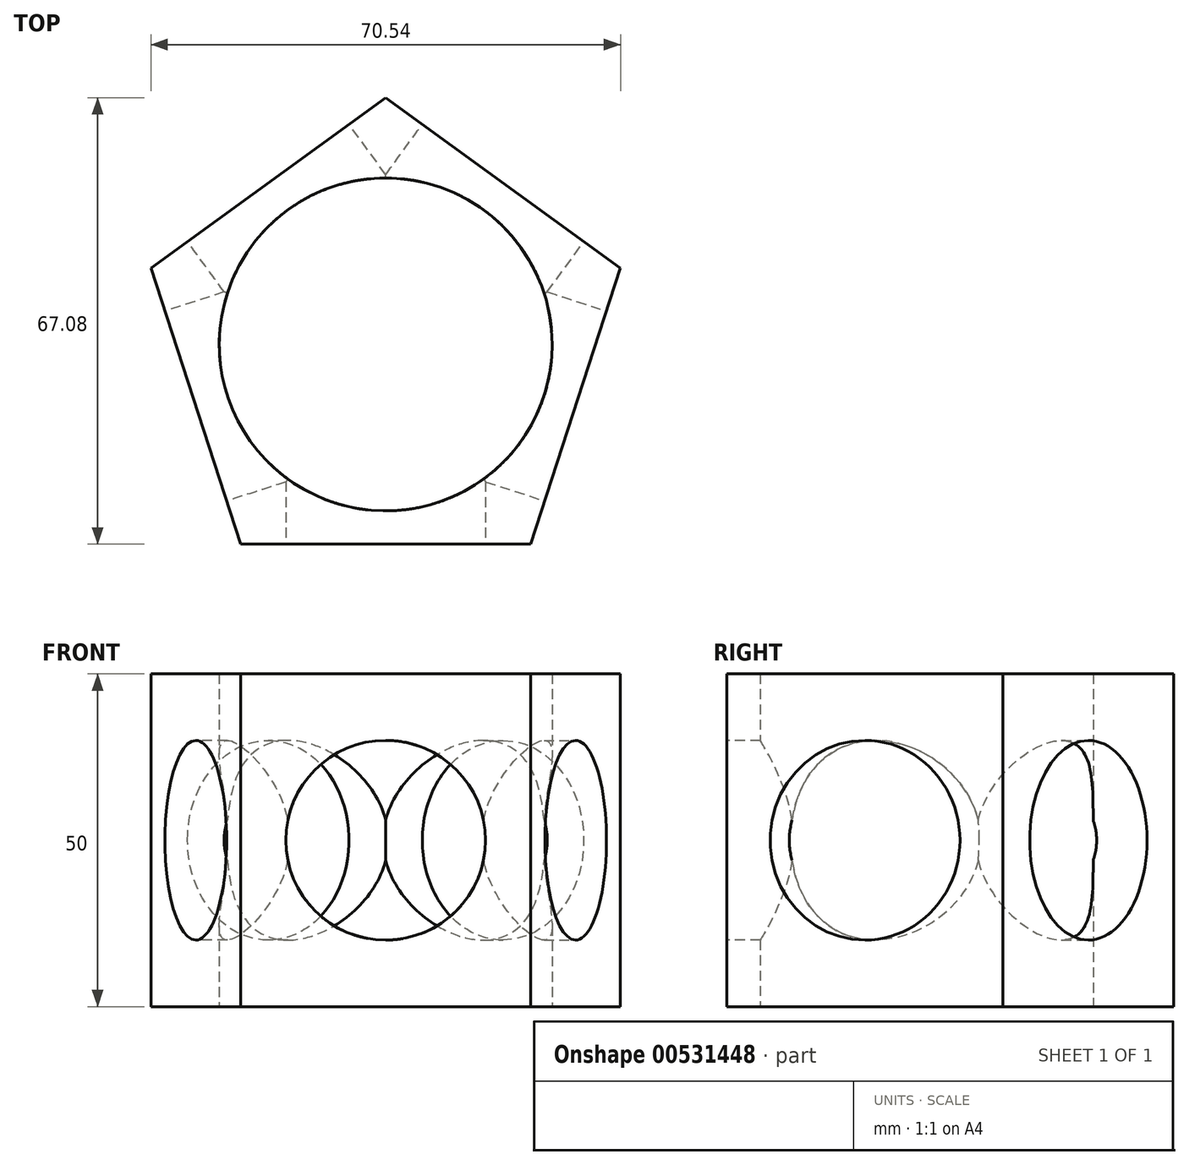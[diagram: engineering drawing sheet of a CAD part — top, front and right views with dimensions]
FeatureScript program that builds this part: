
annotation { "Feature Type Name" : "Feature", "Feature Type Description" : "" }
export const myFeature = defineFeature(function(context is Context, id is Id, definition is map)
    precondition{}
    {
        {
            var Q0;
            Q0=qCreatedBy(makeId("Top.planeOp"),FACE);
            var sketch = newSketch(context, id + "F0", { "sketchPlane" : qUnion([Q0])});
            skCircle(sketch, "E0.cCircle", {"center": v(0, 0) * mm, "radius": 30 * mm, "construction": true});
            skLineSegment(sketch, "E0.0", {"start": v(-35.27, 11.46) * mm, "end": v(0, 37.08) * mm});
            skLineSegment(sketch, "E0.1", {"start": v(0, 37.08) * mm, "end": v(35.27, 11.46) * mm});
            skLineSegment(sketch, "E0.2", {"start": v(35.27, 11.46) * mm, "end": v(21.8, -30) * mm});
            skLineSegment(sketch, "E0.3", {"start": v(21.8, -30) * mm, "end": v(-21.8, -30) * mm});
            skLineSegment(sketch, "E0.4", {"start": v(-21.8, -30) * mm, "end": v(-35.27, 11.46) * mm});
            skPoint(sketch, "E0.0.midPoint", {"position": v(-17.63, 24.27) * mm});
            skCircle(sketch, "E1", {"center": v(0, 0) * mm, "radius": 25 * mm});
            skSolve(sketch);
        }
        {
            var Q0;
            Q0 = qSketchRegion(id + "F0", true);
            extrude(context, id + "F1", {"entities" : qUnion([Q0]), "depth" : 50 * mm, "offsetDistance" : 25 * mm});
        }
        {
            var Q0;
            Q0=makeQuery(id+"F1.opExtrude","SWEPT_FACE",FACE,{"disambiguationData":[OSD([sQuery(id+"F0.wireOp",EDGE,"E0.0")])]});
            var sketch = newSketch(context, id + "F2", { "sketchPlane" : qUnion([Q0])});
            skCircle(sketch, "E2", {"center": v(0, 25) * mm, "radius": 15 * mm});
            skPoint(sketch, "E2.centerSnap0", {"position": v(21.8, 25) * mm});
            skPoint(sketch, "E2.centerSnap1", {"position": v(0, 50) * mm});
            skSolve(sketch);
        }
        {
            var Q0;
            Q0 = qSketchRegion(id + "F2", true);
            extrude(context, id + "F3", {"entities" : qUnion([Q0]), "operationType" : NewBodyOperationType.REMOVE, "oppositeDirection" : true, "depth" : 17.7 * mm, "offsetDistance" : 25 * mm});
        }
        {
            var Q0;
            Q0=makeQuery(id+"F1.opExtrude","SWEPT_FACE",FACE,{"disambiguationData":[OSD([sQuery(id+"F0.wireOp",EDGE,"E0.1")])]});
            var sketch = newSketch(context, id + "F4", { "sketchPlane" : qUnion([Q0])});
            skCircle(sketch, "E3", {"center": v(0, 25) * mm, "radius": 15 * mm});
            skPoint(sketch, "E3.centerSnap0", {"position": v(21.8, 25) * mm});
            skSolve(sketch);
        }
        {
            var Q0;
            Q0 = qSketchRegion(id + "F4", true);
            extrude(context, id + "F5", {"entities" : qUnion([Q0]), "operationType" : NewBodyOperationType.REMOVE, "oppositeDirection" : true, "depth" : 15.9 * mm, "offsetDistance" : 25 * mm});
        }
        {
            var Q0;
            Q0=makeQuery(id+"F1.opExtrude","SWEPT_FACE",FACE,{"disambiguationData":[OSD([sQuery(id+"F0.wireOp",EDGE,"E0.2")])]});
            var sketch = newSketch(context, id + "F6", { "sketchPlane" : qUnion([Q0])});
            skCircle(sketch, "E4", {"center": v(0, 25) * mm, "radius": 15 * mm});
            skPoint(sketch, "E4.centerSnap0", {"position": v(21.8, 25) * mm});
            skSolve(sketch);
        }
        {
            var Q0;
            Q0 = qSketchRegion(id + "F6", true);
            extrude(context, id + "F7", {"entities" : qUnion([Q0]), "operationType" : NewBodyOperationType.REMOVE, "oppositeDirection" : true, "depth" : 16 * mm, "offsetDistance" : 25 * mm});
        }
        {
            var Q0;
            Q0=makeQuery(id+"F1.opExtrude","SWEPT_FACE",FACE,{"disambiguationData":[OSD([sQuery(id+"F0.wireOp",EDGE,"E0.3")])]});
            var sketch = newSketch(context, id + "F8", { "sketchPlane" : qUnion([Q0])});
            skCircle(sketch, "E5", {"center": v(0, 25) * mm, "radius": 15 * mm});
            skPoint(sketch, "E5.centerSnap0", {"position": v(21.8, 25) * mm});
            skSolve(sketch);
        }
        {
            var Q0;
            Q0 = qSketchRegion(id + "F8", true);
            extrude(context, id + "F9", {"entities" : qUnion([Q0]), "operationType" : NewBodyOperationType.REMOVE, "oppositeDirection" : true, "depth" : 16 * mm, "offsetDistance" : 25 * mm});
        }
        {
            var Q0;
            Q0=makeQuery(id+"F1.opExtrude","SWEPT_FACE",FACE,{"disambiguationData":[OSD([sQuery(id+"F0.wireOp",EDGE,"E0.4")])]});
            var sketch = newSketch(context, id + "F10", { "sketchPlane" : qUnion([Q0])});
            skCircle(sketch, "E6", {"center": v(0, 25) * mm, "radius": 15 * mm});
            skPoint(sketch, "E6.centerSnap0", {"position": v(21.8, 25) * mm});
            skSolve(sketch);
        }
        {
            var Q0;
            Q0 = qSketchRegion(id + "F10", true);
            extrude(context, id + "F11", {"entities" : qUnion([Q0]), "operationType" : NewBodyOperationType.REMOVE, "oppositeDirection" : true, "depth" : 16 * mm, "offsetDistance" : 25 * mm});
        }
    });
